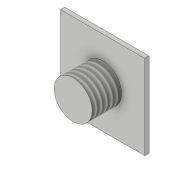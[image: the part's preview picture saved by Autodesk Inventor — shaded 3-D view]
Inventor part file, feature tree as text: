
AUTODESK INVENTOR PART (.ipt)
format: ipt  version: 2019 (Build 230136000, 136)  size: 91,648 bytes
history: native  units: mm
features: extrude x2, sketch x2, thread x1
ambient origin geometry x8: Origin, YZ Plane, XZ Plane, XY Plane, X Axis, Y Axis, Z Axis, Center Point
bodies: Solid1 (feature_tree)
feature tree (5):
  extrude  "Extrusion1"  Depth=20.0mm
  extrude  "Extrusion2"  Depth=10.0mm
  thread  "Thread1"  [1 undecoded]
  sketch  "Sketch1"  dims[d0=20.0mm d1=20.0mm]
  sketch  "Sketch2"  dims[d2=1.0mm d3=0.0mm d4=10.0mm d5=10.0mm d6=9.0mm d7=7.0mm d8=0.0mm d9=10.0mm d10=0.0mm]
note: 1 required parameter value undecoded (feature->parameter linkage not recoverable at this tier; creation-order binding heuristic only, values carry confidence <= 0.55)
